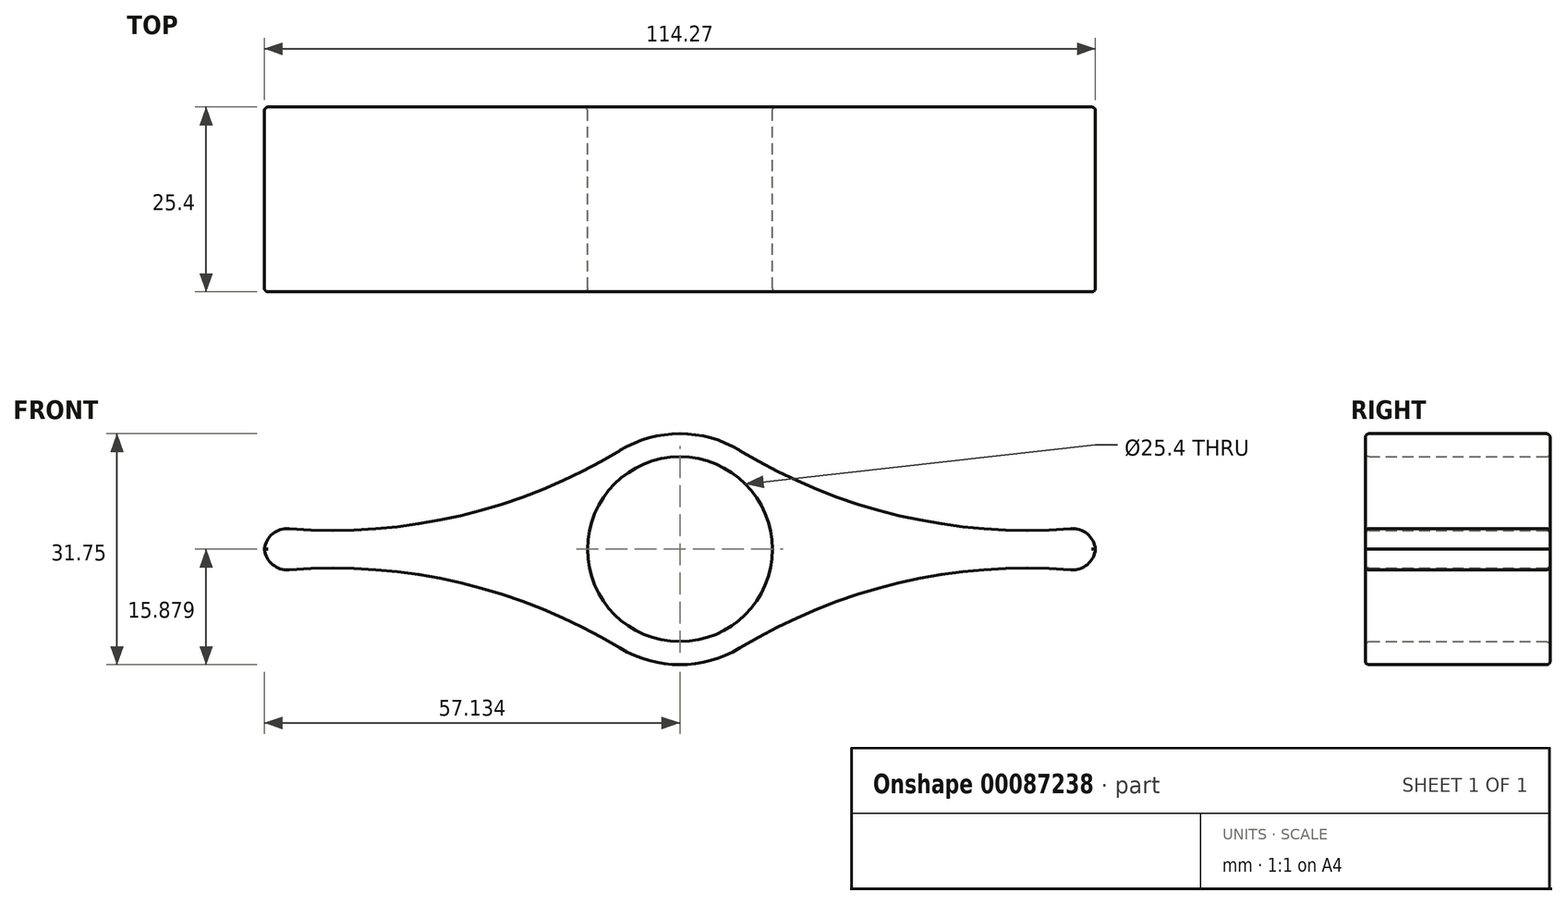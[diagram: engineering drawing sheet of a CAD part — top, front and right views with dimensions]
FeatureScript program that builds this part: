
annotation { "Feature Type Name" : "Feature", "Feature Type Description" : "" }
export const myFeature = defineFeature(function(context is Context, id is Id, definition is map)
    precondition{}
    {
        {
            var Q0;
            Q0=qCreatedBy(makeId("Front.planeOp"),FACE);
            var sketch = newSketch(context, id + "F0", { "sketchPlane" : qUnion([Q0])});
            skCircle(sketch, "E0", {"center": v(-41.59, 27.2) * mm, "radius": 12.7 * mm});
            skCircle(sketch, "E1", {"center": v(-41.59, 27.2) * mm, "radius": 15.88 * mm});
            skLineSegment(sketch, "E2", {"start": v(-41.59, 27.2) * mm, "end": v(15.56, 27.2) * mm, "construction": true});
            skLineSegment(sketch, "E3", {"start": v(15.56, 27.2) * mm, "end": v(15.56, 30.37) * mm});
            skArc(sketch, "E4", {"start": v(-33.37, 40.78) * mm, "mid": v(-9.78, 31.45) * mm, "end": v(15.56, 30.37) * mm});
            skArc(sketch, "E5.MirrorCS", {"start": v(-33.37, 13.62) * mm, "mid": v(-9.78, 22.95) * mm, "end": v(15.56, 24.02) * mm});
            skLineSegment(sketch, "E6", {"start": v(-41.59, 27.2) * mm, "end": v(-41.59, 43.07) * mm, "construction": true});
            skArc(sketch, "E7.MirrorCS", {"start": v(-49.8, 40.78) * mm, "mid": v(-73.4, 31.45) * mm, "end": v(-98.74, 30.37) * mm});
            skArc(sketch, "E8.MirrorCS", {"start": v(-49.8, 13.62) * mm, "mid": v(-73.4, 22.95) * mm, "end": v(-98.74, 24.02) * mm});
            skLineSegment(sketch, "E9.MirrorCS", {"start": v(-98.74, 27.2) * mm, "end": v(-98.74, 30.37) * mm});
            skLineSegment(sketch, "E10.MirrorCS", {"start": v(15.56, 27.2) * mm, "end": v(15.56, 24.02) * mm});
            skLineSegment(sketch, "E11.MirrorCS", {"start": v(-98.74, 27.2) * mm, "end": v(-98.74, 24.02) * mm});
            skSolve(sketch);
        }
        {
            var Q0;
            Q0 = qSketchRegion(id + "F0", true);
            extrude(context, id + "F1", {"entities" : qUnion([Q0]), "depth" : 25.4 * mm});
        }
        {
            var Q0;
            Q0=makeQuery(id+"F1.opExtrude","SWEPT_EDGE",EDGE,{"disambiguationData":[OSD([sQuery(id+"F0.wireOp",EDGE,"E3"),sQuery(id+"F0.wireOp",EDGE,"E4")])]});
            var Q1;
            Q1=makeQuery(id+"F1.opExtrude","SWEPT_EDGE",EDGE,{"disambiguationData":[OSD([sQuery(id+"F0.wireOp",EDGE,"E5.MirrorCS"),sQuery(id+"F0.wireOp",EDGE,"E10.MirrorCS")])]});
            var Q2;
            Q2=makeQuery(id+"F1.opExtrude","SWEPT_EDGE",EDGE,{"disambiguationData":[OSD([sQuery(id+"F0.wireOp",EDGE,"E7.MirrorCS"),sQuery(id+"F0.wireOp",EDGE,"E9.MirrorCS")])]});
            var Q3;
            Q3=makeQuery(id+"F1.opExtrude","SWEPT_EDGE",EDGE,{"disambiguationData":[OSD([sQuery(id+"F0.wireOp",EDGE,"E8.MirrorCS"),sQuery(id+"F0.wireOp",EDGE,"E11.MirrorCS")])]});
            fillet(context, id + "F2", {"entities" : qUnion([Q0, Q1, Q2, Q3]), "radius" : 3.17 * mm, "tangentPropagation" : true, "defaultsChanged" : false, "vertexSettings" : [], "allowEdgeOverflow" : false});
        }
        {
            var Q0;
            Q0=makeQuery(id+"F1.opExtrude","CAP_EDGE",EDGE,{"disambiguationData":[OSD([sQuery(id+"F0.wireOp",EDGE,"E7.MirrorCS")])],"isStart":false});
            var Q1;
            Q1=makeQuery(id+"F1.opExtrude","CAP_EDGE",EDGE,{"disambiguationData":[OSD([sQuery(id+"F0.wireOp",EDGE,"E4")])],"isStart":true});
            var Q2;
            Q2=makeQuery(id+"F1.opExtrude","CAP_EDGE",EDGE,{"disambiguationData":[OSD([sQuery(id+"F0.wireOp",EDGE,"E5.MirrorCS")])],"isStart":false});
            var Q3;
            Q3=makeQuery(id+"F1.opExtrude","CAP_EDGE",EDGE,{"disambiguationData":[OSD([sQuery(id+"F0.wireOp",EDGE,"E5.MirrorCS")])],"isStart":true});
            var Q4;
            Q4=makeQuery(id+"F1.opExtrude","CAP_EDGE",EDGE,{"disambiguationData":[OSD([sQuery(id+"F0.wireOp",EDGE,"E0")])],"isStart":false});
            var Q5;
            Q5=makeQuery(id+"F1.opExtrude","CAP_EDGE",EDGE,{"disambiguationData":[OSD([sQuery(id+"F0.wireOp",EDGE,"E0")])],"isStart":true});
            fillet(context, id + "F3", {"entities" : qUnion([Q0, Q1, Q2, Q3, Q4, Q5]), "radius" : 0.5 * mm, "tangentPropagation" : true, "defaultsChanged" : false, "vertexSettings" : [], "allowEdgeOverflow" : false});
        }
    });
